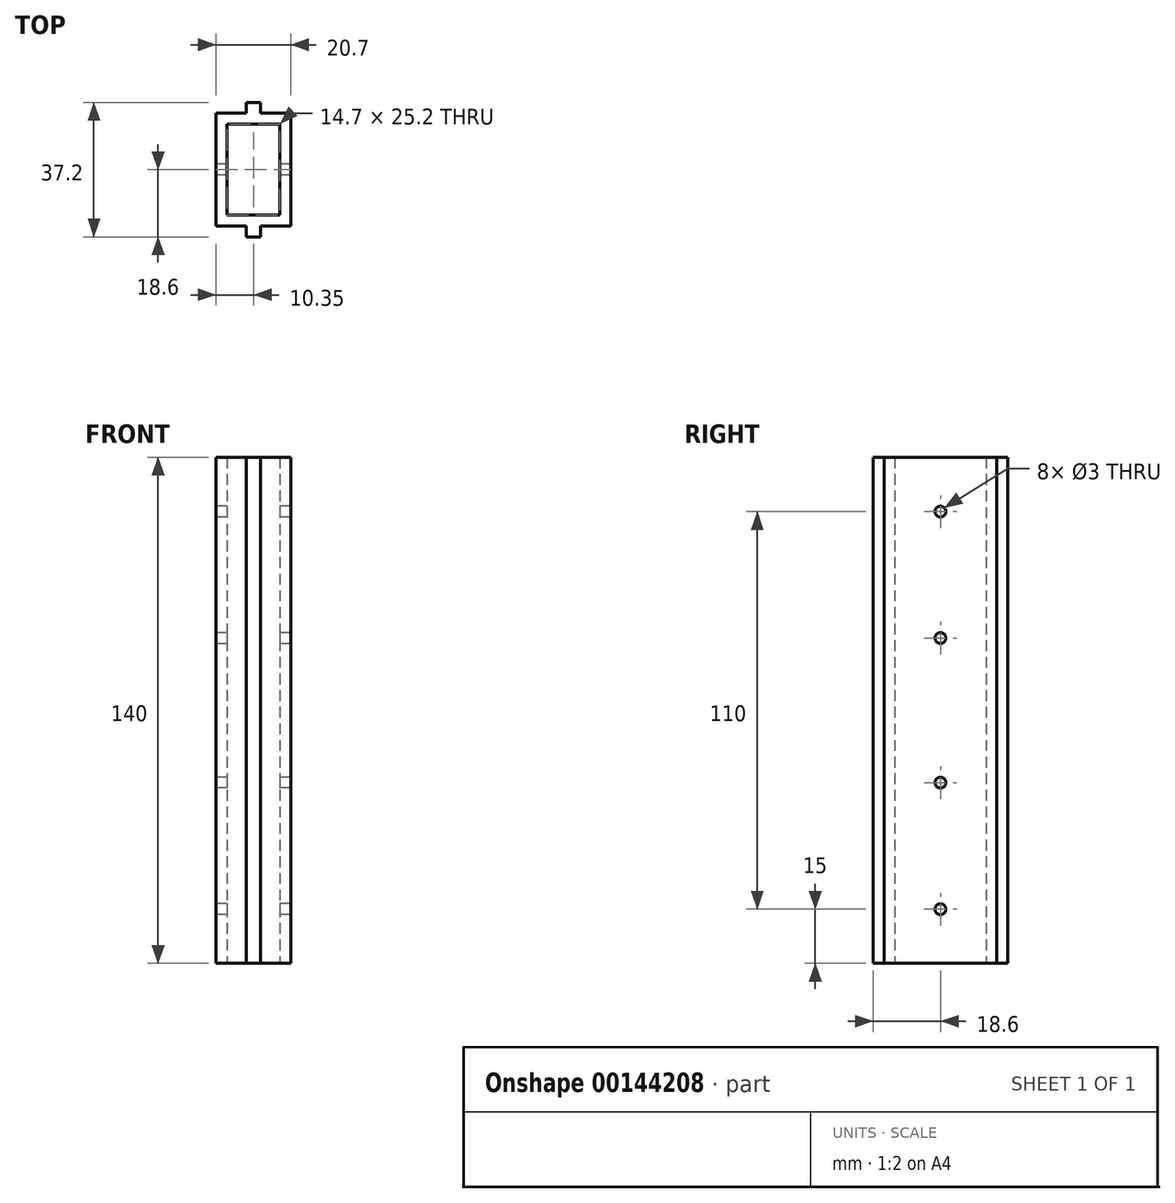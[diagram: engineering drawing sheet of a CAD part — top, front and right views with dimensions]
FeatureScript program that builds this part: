
annotation { "Feature Type Name" : "Feature", "Feature Type Description" : "" }
export const myFeature = defineFeature(function(context is Context, id is Id, definition is map)
    precondition{}
    {
        {
            var Q0;
            Q0=qCreatedBy(makeId("Top.planeOp"),FACE);
            var sketch = newSketch(context, id + "F0", { "sketchPlane" : qUnion([Q0])});
            skLineSegment(sketch, "E0.bottom", {"start": v(7.35, -12.6) * mm, "end": v(-7.35, -12.6) * mm});
            skLineSegment(sketch, "E0.top", {"start": v(7.35, 12.6) * mm, "end": v(-7.35, 12.6) * mm});
            skLineSegment(sketch, "E0.left", {"start": v(7.35, -12.6) * mm, "end": v(7.35, 12.6) * mm});
            skLineSegment(sketch, "E0.right", {"start": v(-7.35, -12.6) * mm, "end": v(-7.35, 12.6) * mm});
            skPoint(sketch, "E0.middle", {"position": v(0, 0) * mm});
            skLineSegment(sketch, "E1.bottom", {"start": v(10.35, -15.6) * mm, "end": v(-10.35, -15.6) * mm});
            skLineSegment(sketch, "E1.top", {"start": v(10.35, 15.6) * mm, "end": v(-10.35, 15.6) * mm});
            skLineSegment(sketch, "E1.left", {"start": v(10.35, -15.6) * mm, "end": v(10.35, 15.6) * mm});
            skLineSegment(sketch, "E1.right", {"start": v(-10.35, -15.6) * mm, "end": v(-10.35, 15.6) * mm});
            skPoint(sketch, "E2.middle", {"position": v(0, 15.6) * mm});
            skLineSegment(sketch, "E3", {"start": v(-2, -15.6) * mm, "end": v(-2, -18.6) * mm});
            skLineSegment(sketch, "E4", {"start": v(-2, -18.6) * mm, "end": v(0, -18.6) * mm});
            skLineSegment(sketch, "E5.MirrorCS", {"start": v(2, -18.6) * mm, "end": v(0, -18.6) * mm});
            skLineSegment(sketch, "E6.MirrorCS", {"start": v(2, -15.6) * mm, "end": v(2, -18.6) * mm});
            skLineSegment(sketch, "E7.MirrorCS", {"start": v(-2, 15.6) * mm, "end": v(-2, 18.6) * mm});
            skLineSegment(sketch, "E8.MirrorCS", {"start": v(2, 15.6) * mm, "end": v(2, 18.6) * mm});
            skLineSegment(sketch, "E9.MirrorCS", {"start": v(-2, 18.6) * mm, "end": v(0, 18.6) * mm});
            skLineSegment(sketch, "E10.MirrorCS", {"start": v(2, 18.6) * mm, "end": v(0, 18.6) * mm});
            skSolve(sketch);
        }
        {
            var Q0;
            Q0=makeQuery(id+"F0.imprint","IMPRINT",FACE,{"disambiguationData":[TD([[makeQuery(id+"F0.imprint","IMPRINT",EDGE,{"derivedFrom":sQuery(id+"F0.wireOp",EDGE,"E0.top")}),-1.0]])]});
            var Q1;
            {var subQ0=sQuery(id+"F0.wireOp",EDGE,"E3");Q1=makeQuery(id+"F0.imprint","IMPRINT",FACE,{"disambiguationData":[TD([[makeQuery(id+"F0.imprint","IMPRINT",EDGE,{"derivedFrom":subQ0}),1.0]])]});}
            var Q2;
            {var subQ1=sQuery(id+"F0.wireOp",EDGE,"E7.MirrorCS");Q2=makeQuery(id+"F0.imprint","IMPRINT",FACE,{"disambiguationData":[TD([[makeQuery(id+"F0.imprint","IMPRINT",EDGE,{"derivedFrom":subQ1}),-1.0]])]});}
            extrude(context, id + "F1", {"entities" : qUnion([Q0, Q1, Q2]), "depth" : 140 * mm});
        }
        {
            var Q0;
            Q0=makeQuery(id+"F1.opExtrude","SWEPT_FACE",FACE,{"disambiguationData":[OSD([sQuery(id+"F0.wireOp",EDGE,"E1.right")])]});
            var sketch = newSketch(context, id + "F2", { "sketchPlane" : qUnion([Q0])});
            skCircle(sketch, "E11", {"center": v(0, 15) * mm, "radius": 1.44 * mm});
            skCircle(sketch, "E12", {"center": v(0, 50) * mm, "radius": 1.73 * mm});
            skCircle(sketch, "E13", {"center": v(0, 90) * mm, "radius": 1.43 * mm});
            skCircle(sketch, "E14", {"center": v(0, 125) * mm, "radius": 1.44 * mm});
            skSolve(sketch);
        }
        {
            var Q0;
            Q0=sQuery(id+"F2.wireOp",VERTEX,"E11.center");
            var Q1;
            Q1=sQuery(id+"F2.wireOp",VERTEX,"E12.center");
            var Q2;
            Q2=sQuery(id+"F2.wireOp",VERTEX,"E13.center");
            var Q3;
            Q3=sQuery(id+"F2.wireOp",VERTEX,"E14.center");
            var Q4;
            Q4=makeQuery(id+"F1.opExtrude","SWEPT_BODY",BODY,{"disambiguationData":[OSD([sQuery(id+"F0.wireOp",EDGE,"E0.top"),sQuery(id+"F0.wireOp",EDGE,"E0.left"),sQuery(id+"F0.wireOp",EDGE,"E0.right"),sQuery(id+"F0.wireOp",EDGE,"E1.bottom"),sQuery(id+"F0.wireOp",EDGE,"E1.top"),sQuery(id+"F0.wireOp",EDGE,"E1.left"),sQuery(id+"F0.wireOp",EDGE,"E1.right"),sQuery(id+"F0.wireOp",EDGE,"E2.top"),sQuery(id+"F0.wireOp",EDGE,"E2.left"),sQuery(id+"F0.wireOp",EDGE,"E2.right"),sQuery(id+"F0.wireOp",EDGE,"20c965e6-ac80-4f75-bf15-646049ae776c0.MirrorCS"),sQuery(id+"F0.wireOp",EDGE,"075c9b09-a2b1-46ac-9159-c5ca6d48e2e50.MirrorCS"),sQuery(id+"F0.wireOp",EDGE,"E0.bottom"),sQuery(id+"F0.wireOp",EDGE,"6405ebce-d483-4929-b91f-e80c920d07c20.MirrorCS")])]});
            hole(context, id + "F3", {"style" : HoleStyle.SIMPLE, "endStyle" : HoleEndStyle.THROUGH, "holeDiameter" : 3 * mm, "locations" : qUnion([Q0, Q1, Q2, Q3]), "scope" : qUnion([Q4]), "isTappedThrough" : true});
        }
    });
